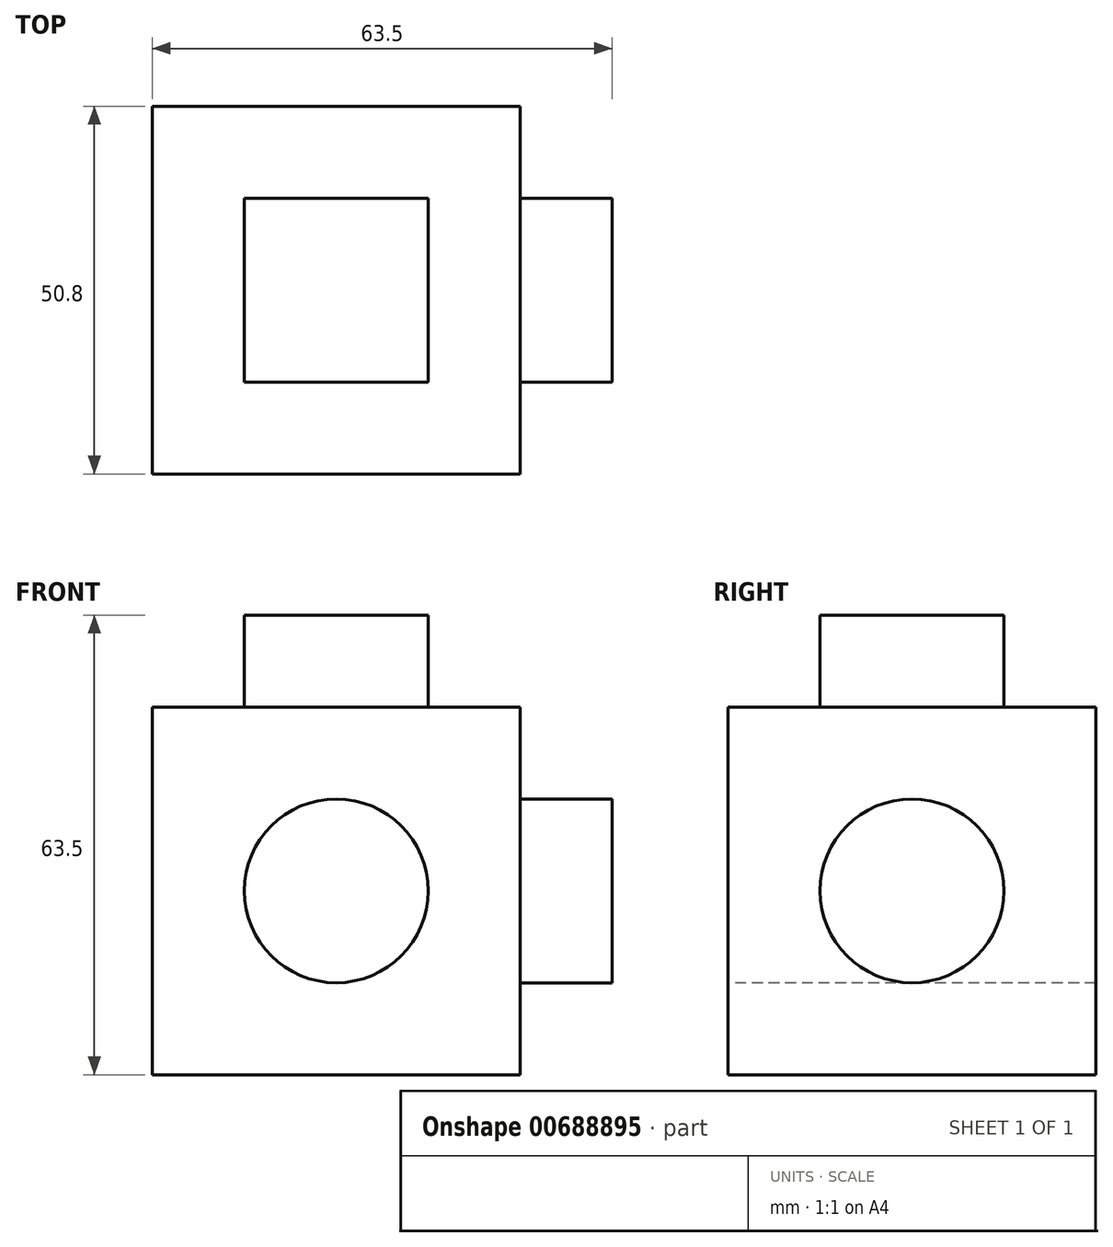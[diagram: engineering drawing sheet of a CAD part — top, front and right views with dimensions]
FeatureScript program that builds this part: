
annotation { "Feature Type Name" : "Feature", "Feature Type Description" : "" }
export const myFeature = defineFeature(function(context is Context, id is Id, definition is map)
    precondition{}
    {
        {
            var Q0;
            Q0=qCreatedBy(makeId("Front.planeOp"),FACE);
            var sketch = newSketch(context, id + "F0", { "sketchPlane" : qUnion([Q0])});
            skLineSegment(sketch, "E0.bottom", {"start": v(-46.24, 32.25) * mm, "end": v(4.56, 32.25) * mm});
            skLineSegment(sketch, "E0.top", {"start": v(-46.24, -18.55) * mm, "end": v(4.56, -18.55) * mm});
            skLineSegment(sketch, "E0.left", {"start": v(-46.24, 32.25) * mm, "end": v(-46.24, -18.55) * mm});
            skLineSegment(sketch, "E0.right", {"start": v(4.56, 32.25) * mm, "end": v(4.56, -18.55) * mm});
            skSolve(sketch);
        }
        {
            var Q0;
            Q0=makeQuery(id+"F0.imprint","IMPRINT",FACE,{"disambiguationData":[TD([[makeQuery(id+"F0.imprint","IMPRINT",EDGE,{"derivedFrom":sQuery(id+"F0.wireOp",EDGE,"E0.bottom")}),-1.0]])]});
            extrude(context, id + "F1", {"entities" : qUnion([Q0]), "depth" : 50.8 * mm, "offsetDistance" : 25.4 * mm});
        }
        {
            var Q0;
            Q0=makeQuery(id+"F1.opExtrude","CAP_FACE",FACE,{"disambiguationData":[OSD([sQuery(id+"F0.wireOp",EDGE,"E0.bottom"),sQuery(id+"F0.wireOp",EDGE,"E0.top"),sQuery(id+"F0.wireOp",EDGE,"E0.left"),sQuery(id+"F0.wireOp",EDGE,"E0.right")])],"isStart":false});
            var sketch = newSketch(context, id + "F2", { "sketchPlane" : qUnion([Q0])});
            skCircle(sketch, "E1", {"center": v(-20.84, 6.85) * mm, "radius": 12.7 * mm});
            skSolve(sketch);
        }
        {
            var Q0;
            Q0=makeQuery(id+"F2.imprint","IMPRINT",FACE,{"disambiguationData":[TD([[makeQuery(id+"F2.imprint","IMPRINT",EDGE,{"derivedFrom":sQuery(id+"F2.wireOp",EDGE,"E1")}),1.0]])]});
            extrude(context, id + "F3", {"entities" : qUnion([Q0]), "operationType" : NewBodyOperationType.REMOVE, "oppositeDirection" : true, "depth" : 50.8 * mm, "offsetDistance" : 25.4 * mm});
        }
        {
            var Q0;
            Q0=makeQuery(id+"F1.opExtrude","SWEPT_FACE",FACE,{"disambiguationData":[OSD([sQuery(id+"F0.wireOp",EDGE,"E0.bottom")])]});
            var sketch = newSketch(context, id + "F4", { "sketchPlane" : qUnion([Q0])});
            skLineSegment(sketch, "E2.bottom", {"start": v(-33.54, -12.7) * mm, "end": v(-8.14, -12.7) * mm});
            skLineSegment(sketch, "E2.top", {"start": v(-33.54, -38.1) * mm, "end": v(-8.14, -38.1) * mm});
            skLineSegment(sketch, "E2.left", {"start": v(-33.54, -12.7) * mm, "end": v(-33.54, -38.1) * mm});
            skLineSegment(sketch, "E2.right", {"start": v(-8.14, -12.7) * mm, "end": v(-8.14, -38.1) * mm});
            skSolve(sketch);
        }
        {
            var Q0;
            Q0=makeQuery(id+"F4.imprint","IMPRINT",FACE,{"disambiguationData":[TD([[makeQuery(id+"F4.imprint","IMPRINT",EDGE,{"derivedFrom":sQuery(id+"F4.wireOp",EDGE,"E2.bottom")}),-1.0]])]});
            extrude(context, id + "F5", {"entities" : qUnion([Q0]), "operationType" : NewBodyOperationType.ADD, "depth" : 12.7 * mm, "offsetDistance" : 25.4 * mm});
        }
        {
            var Q0;
            Q0=makeQuery(id+"F1.opExtrude","SWEPT_FACE",FACE,{"disambiguationData":[OSD([sQuery(id+"F0.wireOp",EDGE,"E0.right")])]});
            var sketch = newSketch(context, id + "F6", { "sketchPlane" : qUnion([Q0])});
            skCircle(sketch, "E3", {"center": v(-25.4, 6.85) * mm, "radius": 12.7 * mm});
            skSolve(sketch);
        }
        {
            var Q0;
            Q0=makeQuery(id+"F6.imprint","IMPRINT",FACE,{"disambiguationData":[TD([[makeQuery(id+"F6.imprint","IMPRINT",EDGE,{"derivedFrom":sQuery(id+"F6.wireOp",EDGE,"E3")}),1.0]])]});
            extrude(context, id + "F7", {"entities" : qUnion([Q0]), "operationType" : NewBodyOperationType.ADD, "depth" : 12.7 * mm, "offsetDistance" : 25.4 * mm});
        }
    });
